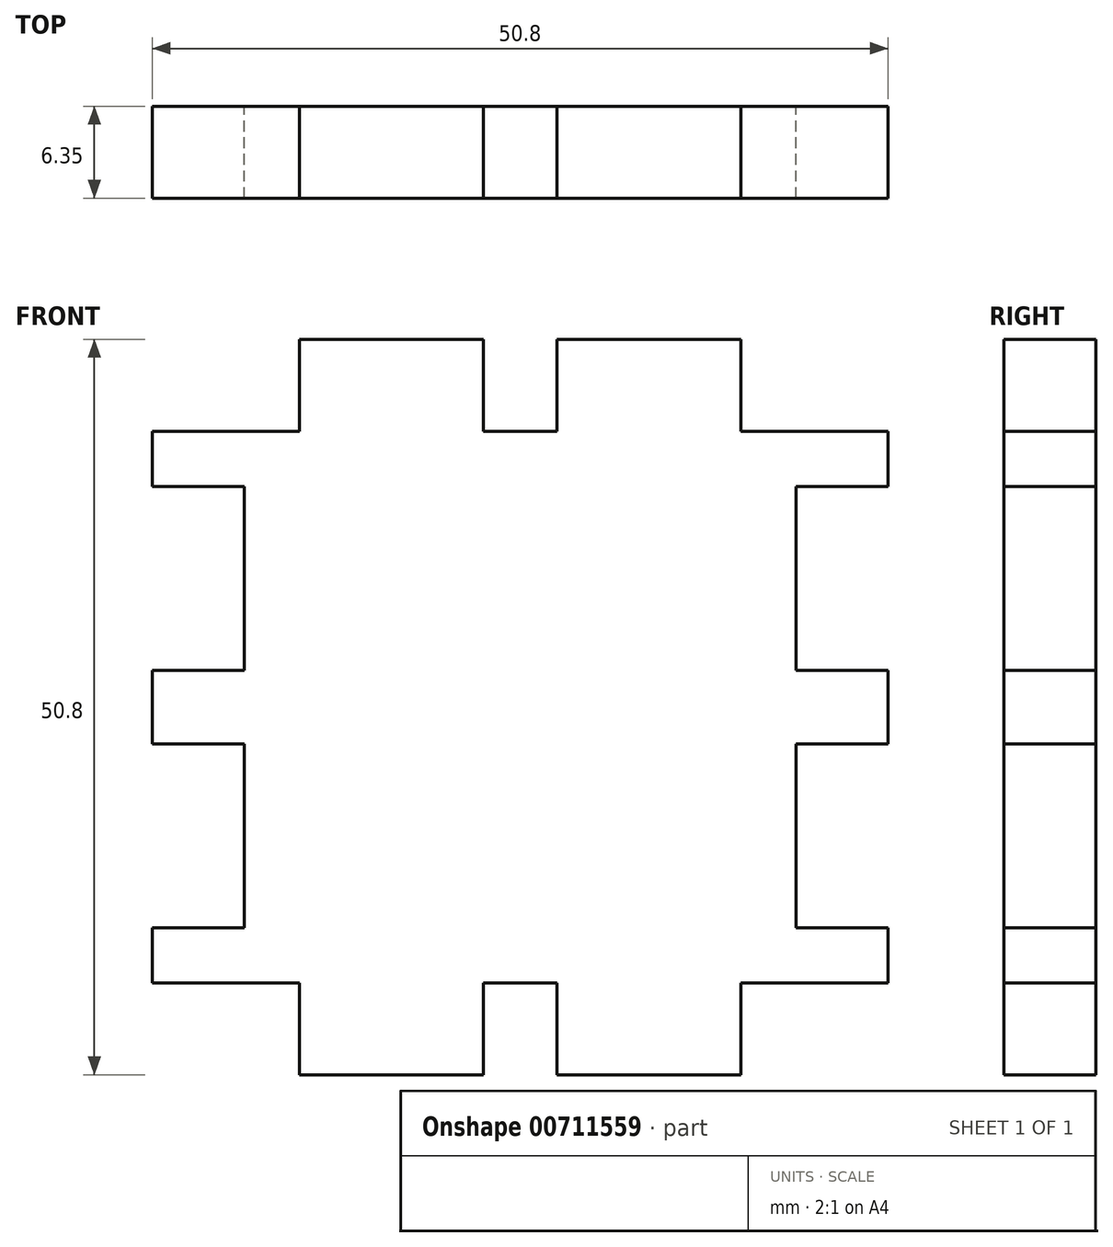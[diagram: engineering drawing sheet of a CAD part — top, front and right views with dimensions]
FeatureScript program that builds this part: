
annotation { "Feature Type Name" : "Feature", "Feature Type Description" : "" }
export const myFeature = defineFeature(function(context is Context, id is Id, definition is map)
    precondition{}
    {
        {
            var Q0;
            Q0=qCreatedBy(makeId("Front.planeOp"),FACE);
            var sketch = newSketch(context, id + "F0", { "sketchPlane" : qUnion([Q0])});
            skLineSegment(sketch, "E0.bottom", {"start": v(25.4, 25.4) * mm, "end": v(-25.4, 25.4) * mm, "construction": true});
            skLineSegment(sketch, "E0.top", {"start": v(25.4, -25.4) * mm, "end": v(-25.4, -25.4) * mm, "construction": true});
            skLineSegment(sketch, "E0.left", {"start": v(25.4, 25.4) * mm, "end": v(25.4, -25.4) * mm, "construction": true});
            skLineSegment(sketch, "E0.right", {"start": v(-25.4, 25.4) * mm, "end": v(-25.4, -25.4) * mm, "construction": true});
            skPoint(sketch, "E0.middle", {"position": v(0, 0) * mm});
            skLineSegment(sketch, "E1", {"start": v(-15.24, 25.4) * mm, "end": v(-15.24, -25.4) * mm, "construction": true});
            skLineSegment(sketch, "E2", {"start": v(-2.54, 25.4) * mm, "end": v(-2.54, -25.4) * mm, "construction": true});
            skLineSegment(sketch, "E3", {"start": v(2.54, 25.4) * mm, "end": v(2.54, -25.4) * mm, "construction": true});
            skLineSegment(sketch, "E4", {"start": v(15.24, 25.4) * mm, "end": v(15.24, -25.4) * mm, "construction": true});
            skLineSegment(sketch, "E5", {"start": v(25.4, 15.24) * mm, "end": v(-25.4, 15.24) * mm, "construction": true});
            skLineSegment(sketch, "E6", {"start": v(25.4, 2.54) * mm, "end": v(-25.4, 2.54) * mm, "construction": true});
            skLineSegment(sketch, "E7", {"start": v(25.4, -2.54) * mm, "end": v(-25.4, -2.54) * mm, "construction": true});
            skLineSegment(sketch, "E8", {"start": v(-25.4, -15.24) * mm, "end": v(25.4, -15.24) * mm, "construction": true});
            skLineSegment(sketch, "E9", {"start": v(19.05, 25.4) * mm, "end": v(19.05, -25.4) * mm, "construction": true});
            skLineSegment(sketch, "E10", {"start": v(25.4, 19.05) * mm, "end": v(-25.4, 19.05) * mm, "construction": true});
            skLineSegment(sketch, "E11", {"start": v(-19.05, 25.4) * mm, "end": v(-19.05, -25.4) * mm, "construction": true});
            skLineSegment(sketch, "E12", {"start": v(-25.4, -19.05) * mm, "end": v(25.4, -19.05) * mm, "construction": true});
            skLineSegment(sketch, "E13", {"start": v(-15.24, -25.4) * mm, "end": v(-2.54, -25.4) * mm});
            skLineSegment(sketch, "E14", {"start": v(-2.54, -25.4) * mm, "end": v(-2.54, -19.05) * mm});
            skLineSegment(sketch, "E15", {"start": v(-2.54, -19.05) * mm, "end": v(2.54, -19.05) * mm});
            skLineSegment(sketch, "E16", {"start": v(2.54, -19.05) * mm, "end": v(2.54, -25.4) * mm});
            skLineSegment(sketch, "E17", {"start": v(2.54, -25.4) * mm, "end": v(15.24, -25.4) * mm});
            skLineSegment(sketch, "E18", {"start": v(15.24, -19.05) * mm, "end": v(15.24, -25.4) * mm});
            skLineSegment(sketch, "E19", {"start": v(15.24, -19.05) * mm, "end": v(25.4, -19.05) * mm});
            skLineSegment(sketch, "E20", {"start": v(25.4, -19.05) * mm, "end": v(25.4, -15.24) * mm});
            skLineSegment(sketch, "E21", {"start": v(25.4, -15.24) * mm, "end": v(19.05, -15.24) * mm});
            skLineSegment(sketch, "E22", {"start": v(19.05, -15.24) * mm, "end": v(19.05, -2.54) * mm});
            skLineSegment(sketch, "E23", {"start": v(19.05, -2.54) * mm, "end": v(25.4, -2.54) * mm});
            skLineSegment(sketch, "E24", {"start": v(25.4, -2.54) * mm, "end": v(25.4, 2.54) * mm});
            skLineSegment(sketch, "E25", {"start": v(25.4, 2.54) * mm, "end": v(19.05, 2.54) * mm});
            skLineSegment(sketch, "E26", {"start": v(19.05, 2.54) * mm, "end": v(19.05, 15.24) * mm});
            skLineSegment(sketch, "E27", {"start": v(19.05, 15.24) * mm, "end": v(25.4, 15.24) * mm});
            skLineSegment(sketch, "E28", {"start": v(-25.4, 15.24) * mm, "end": v(-19.05, 15.24) * mm});
            skLineSegment(sketch, "E29", {"start": v(-19.05, 15.24) * mm, "end": v(-19.05, 2.54) * mm});
            skLineSegment(sketch, "E30", {"start": v(-19.05, 2.54) * mm, "end": v(-25.4, 2.54) * mm});
            skLineSegment(sketch, "E31", {"start": v(-25.4, 2.54) * mm, "end": v(-25.4, -2.54) * mm});
            skLineSegment(sketch, "E32", {"start": v(-25.4, -2.54) * mm, "end": v(-19.05, -2.54) * mm});
            skLineSegment(sketch, "E33", {"start": v(-19.05, -2.54) * mm, "end": v(-19.05, -15.24) * mm});
            skLineSegment(sketch, "E34", {"start": v(-19.05, -15.24) * mm, "end": v(-25.4, -15.24) * mm});
            skLineSegment(sketch, "E35", {"start": v(-25.4, -15.24) * mm, "end": v(-25.4, -19.05) * mm});
            skLineSegment(sketch, "E36", {"start": v(-25.4, -19.05) * mm, "end": v(-15.24, -19.05) * mm});
            skLineSegment(sketch, "E37", {"start": v(-15.24, -19.05) * mm, "end": v(-15.24, -25.4) * mm});
            skLineSegment(sketch, "E38", {"start": v(-15.24, 19.05) * mm, "end": v(-15.24, 25.4) * mm});
            skLineSegment(sketch, "E39", {"start": v(-15.24, 25.4) * mm, "end": v(-2.54, 25.4) * mm});
            skLineSegment(sketch, "E40", {"start": v(-2.54, 25.4) * mm, "end": v(-2.54, 19.05) * mm});
            skLineSegment(sketch, "E41", {"start": v(-2.54, 19.05) * mm, "end": v(2.54, 19.05) * mm});
            skLineSegment(sketch, "E42", {"start": v(2.54, 19.05) * mm, "end": v(2.54, 25.4) * mm});
            skLineSegment(sketch, "E43", {"start": v(2.54, 25.4) * mm, "end": v(15.24, 25.4) * mm});
            skLineSegment(sketch, "E44", {"start": v(15.24, 25.4) * mm, "end": v(15.24, 19.05) * mm});
            skLineSegment(sketch, "E45", {"start": v(15.24, 19.05) * mm, "end": v(19.05, 19.05) * mm});
            skLineSegment(sketch, "E46", {"start": v(-15.24, 19.05) * mm, "end": v(-19.05, 19.05) * mm});
            skLineSegment(sketch, "E47", {"start": v(25.4, 15.24) * mm, "end": v(25.4, 19.05) * mm});
            skLineSegment(sketch, "E48", {"start": v(25.4, 19.05) * mm, "end": v(19.05, 19.05) * mm});
            skLineSegment(sketch, "E49", {"start": v(-25.4, 15.24) * mm, "end": v(-25.4, 19.05) * mm});
            skLineSegment(sketch, "E50", {"start": v(-25.4, 19.05) * mm, "end": v(-19.05, 19.05) * mm});
            skSolve(sketch);
        }
        {
            var Q0;
            Q0=makeQuery(id+"F0.imprint","IMPRINT",FACE,{"disambiguationData":[TD([[makeQuery(id+"F0.imprint","IMPRINT",EDGE,{"derivedFrom":sQuery(id+"F0.wireOp",EDGE,"E13")}),1.0]])]});
            extrude(context, id + "F1", {"entities" : qUnion([Q0]), "depth" : 6.35 * mm, "offsetDistance" : 25.4 * mm});
        }
    });
